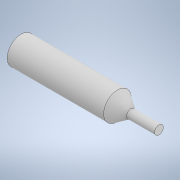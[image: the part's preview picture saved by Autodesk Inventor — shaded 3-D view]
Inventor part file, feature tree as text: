
AUTODESK INVENTOR PART (.ipt)
format: ipt  version: 2021 (Build 250183000, 183)  size: 102,912 bytes
history: native  units: mm
features: revolve x1, sketch x1
ambient origin geometry x8: Origin, YZ Plane, XZ Plane, XY Plane, X Axis, Y Axis, Z Axis, Center Point
bodies: Solid1 (feature_tree)
feature tree (2):
  revolve  "Revolution1"  [1 undecoded]
  sketch  "Sketch1"  dims[d0=15.0mm d1=4.75mm d3=45.157mm d4=21.816616mm d5=150.0mm d6=90.0deg]
note: 1 required parameter value undecoded (feature->parameter linkage not recoverable at this tier; creation-order binding heuristic only, values carry confidence <= 0.55)
